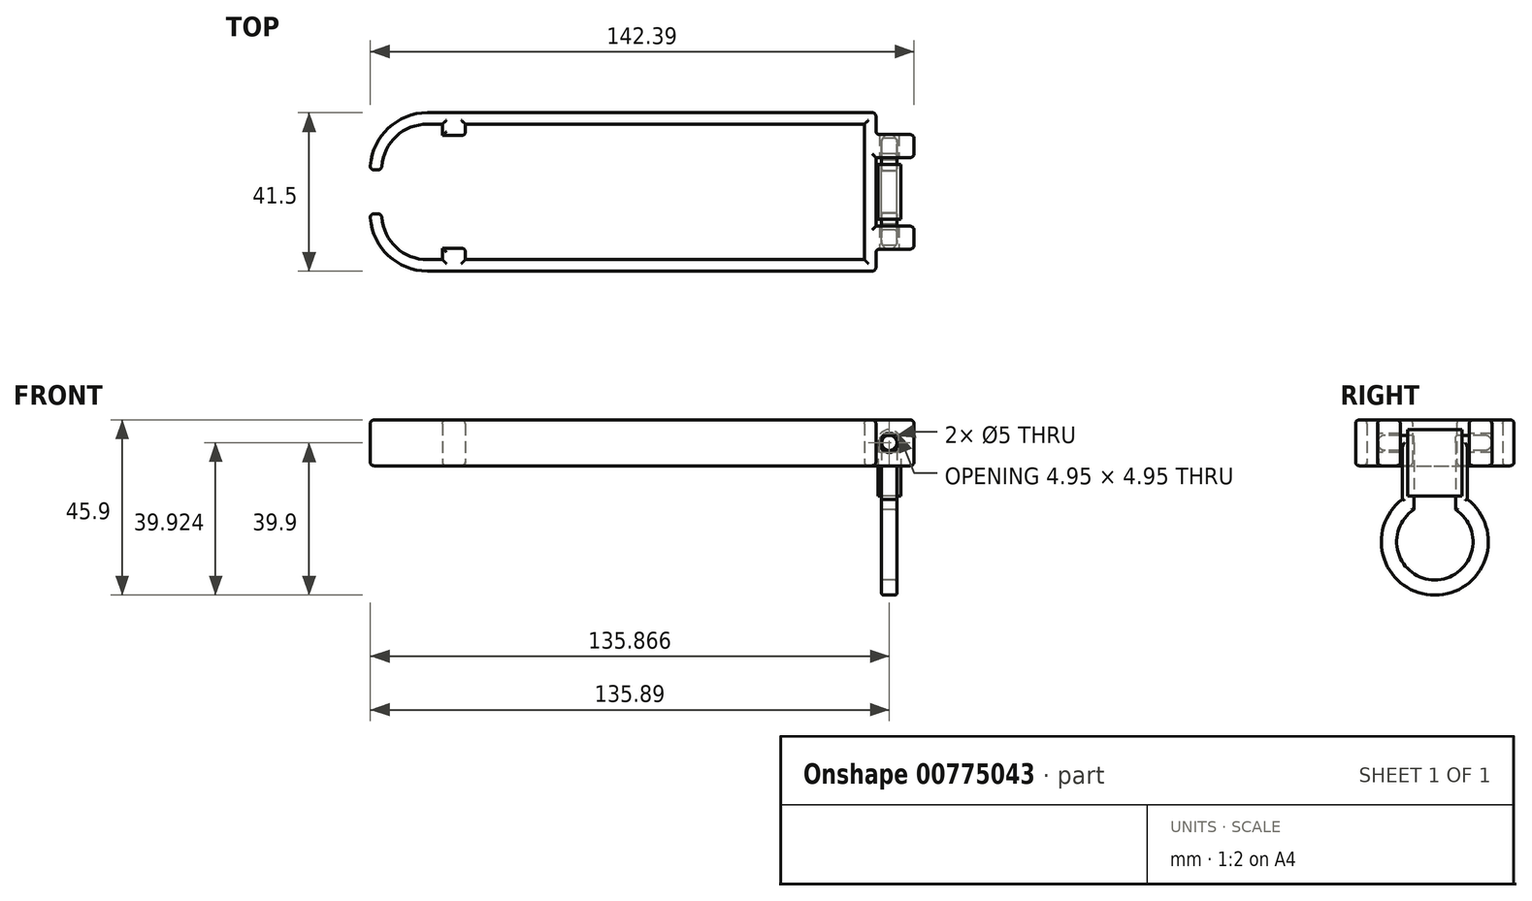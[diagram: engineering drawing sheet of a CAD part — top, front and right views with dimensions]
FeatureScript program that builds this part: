
annotation { "Feature Type Name" : "Feature", "Feature Type Description" : "" }
export const myFeature = defineFeature(function(context is Context, id is Id, definition is map)
    precondition{}
    {
        {
            var Q0;
            Q0=qCreatedBy(makeId("Top.planeOp"),FACE);
            var sketch = newSketch(context, id + "F0", { "sketchPlane" : qUnion([Q0])});
            skLineSegment(sketch, "E0.bottom", {"start": v(0, 0) * mm, "end": v(-104.5, 0) * mm, "construction": true});
            skLineSegment(sketch, "E0.top", {"start": v(0, -35.5) * mm, "end": v(-104.5, -35.5) * mm, "construction": true});
            skLineSegment(sketch, "E0.left", {"start": v(0, 0) * mm, "end": v(0, -35.5) * mm, "construction": true});
            skLineSegment(sketch, "E0.right", {"start": v(-104.5, 0) * mm, "end": v(-104.5, -3) * mm, "construction": true});
            skLineSegment(sketch, "E1.bottom", {"start": v(-104.5, -32.5) * mm, "end": v(-107.5, -32.5) * mm, "construction": true});
            skLineSegment(sketch, "E1.top", {"start": v(-104.5, -3) * mm, "end": v(-107.5, -3) * mm, "construction": true});
            skLineSegment(sketch, "E1.right", {"start": v(-107.5, -32.5) * mm, "end": v(-107.5, -19.25) * mm, "construction": true});
            skLineSegment(sketch, "E2.bottom", {"start": v(-107.5, -16.25) * mm, "end": v(-148.78, -16.25) * mm, "construction": true});
            skLineSegment(sketch, "E2.top", {"start": v(-107.5, -19.25) * mm, "end": v(-148.78, -19.25) * mm, "construction": true});
            skLineSegment(sketch, "E2.right", {"start": v(-148.78, -16.25) * mm, "end": v(-148.78, -19.25) * mm, "construction": true});
            skLineSegment(sketch, "E3.trimOffspring", {"start": v(-107.5, -16.25) * mm, "end": v(-107.5, -3) * mm, "construction": true});
            skLineSegment(sketch, "E4.trimOffspring", {"start": v(-104.5, -32.5) * mm, "end": v(-104.5, -35.5) * mm, "construction": true});
            skSolve(sketch);
        }
        {
            var Q0;
            Q0=qCreatedBy(makeId("Top.planeOp"),FACE);
            var sketch = newSketch(context, id + "F1", { "sketchPlane" : qUnion([Q0])});
            skLineSegment(sketch, "E5.bottom", {"start": v(0, 0) * mm, "end": v(-104.5, 0) * mm});
            skLineSegment(sketch, "E5.top", {"start": v(0, 3) * mm, "end": v(-114.42, 3) * mm});
            skLineSegment(sketch, "E5.left", {"start": v(0, 0) * mm, "end": v(0, 3) * mm});
            skLineSegment(sketch, "E6.bottom", {"start": v(0, -35.5) * mm, "end": v(-104.5, -35.5) * mm});
            skLineSegment(sketch, "E6.top", {"start": v(0, -38.5) * mm, "end": v(-114.42, -38.5) * mm});
            skLineSegment(sketch, "E6.left", {"start": v(0, -35.5) * mm, "end": v(0, -38.5) * mm});
            skLineSegment(sketch, "E7.top", {"start": v(-104.5, -3) * mm, "end": v(-110.5, -3) * mm});
            skLineSegment(sketch, "E7.left", {"start": v(-104.5, 0) * mm, "end": v(-104.5, -3) * mm});
            skLineSegment(sketch, "E7.right", {"start": v(-110.5, 0) * mm, "end": v(-110.5, -3) * mm});
            skLineSegment(sketch, "E8.top", {"start": v(-110.5, -32.5) * mm, "end": v(-104.5, -32.5) * mm});
            skLineSegment(sketch, "E8.left", {"start": v(-110.5, -35.5) * mm, "end": v(-110.5, -32.5) * mm});
            skLineSegment(sketch, "E8.right", {"start": v(-104.5, -35.5) * mm, "end": v(-104.5, -32.5) * mm});
            skArc(sketch, "E9", {"start": v(-114.42, 3) * mm, "mid": v(-125.03, -1.4) * mm, "end": v(-129.42, -12) * mm});
            skArc(sketch, "E10", {"start": v(-114.42, 0) * mm, "mid": v(-122.9, -3.51) * mm, "end": v(-126.42, -12) * mm});
            skLineSegment(sketch, "E11.bottom", {"start": v(-129.42, -12) * mm, "end": v(-126.42, -12) * mm});
            skArc(sketch, "E12", {"start": v(-129.42, -23.5) * mm, "mid": v(-125.03, -34.1) * mm, "end": v(-114.42, -38.5) * mm});
            skArc(sketch, "E13", {"start": v(-126.42, -23.5) * mm, "mid": v(-122.9, -31.99) * mm, "end": v(-114.42, -35.5) * mm});
            skLineSegment(sketch, "E14.bottom", {"start": v(-126.42, -23.5) * mm, "end": v(-129.42, -23.5) * mm});
            skLineSegment(sketch, "E15.trimOffspring", {"start": v(-110.5, -35.5) * mm, "end": v(-114.42, -35.5) * mm});
            skLineSegment(sketch, "E16.trimOffspring", {"start": v(-110.5, 0) * mm, "end": v(-114.42, 0) * mm});
            skLineSegment(sketch, "E17.bottom", {"start": v(0, -38.5) * mm, "end": v(3, -38.5) * mm});
            skLineSegment(sketch, "E17.top", {"start": v(0, 3) * mm, "end": v(3, 3) * mm});
            skLineSegment(sketch, "E17.left", {"start": v(0, -38.5) * mm, "end": v(0, 3) * mm});
            skLineSegment(sketch, "E17.right", {"start": v(3, -38.5) * mm, "end": v(3, -32.75) * mm});
            skLineSegment(sketch, "E18.bottom", {"start": v(13, -2.75) * mm, "end": v(3, -2.75) * mm});
            skLineSegment(sketch, "E18.top", {"start": v(13, -32.75) * mm, "end": v(3, -32.75) * mm});
            skLineSegment(sketch, "E19.bottom", {"start": v(3, -8.75) * mm, "end": v(13, -8.75) * mm});
            skLineSegment(sketch, "E19.top", {"start": v(3, -26.75) * mm, "end": v(13, -26.75) * mm});
            skPoint(sketch, "E19.middle", {"position": v(13, -17.75) * mm});
            skPoint(sketch, "E20.orphan", {"position": v(63.3, -6.49) * mm});
            skPoint(sketch, "E21.trimOffspring.end.orphan", {"position": v(63.3, -28.49) * mm});
            skLineSegment(sketch, "E22.trimOffspring", {"start": v(3, -26.75) * mm, "end": v(3, -8.75) * mm});
            skLineSegment(sketch, "E23.trimOffspring", {"start": v(3, -2.75) * mm, "end": v(3, 3) * mm});
            skLineSegment(sketch, "E24", {"start": v(13, -8.75) * mm, "end": v(13, -2.75) * mm});
            skLineSegment(sketch, "E25", {"start": v(13, -32.75) * mm, "end": v(13, -26.75) * mm});
            skSolve(sketch);
        }
        {
            var Q0;
            Q0=qSketchRegion(id+"F1",true);
            extrude(context, id + "F2", {"entities" : qUnion([Q0]), "depth" : 12 * mm, "offsetDistance" : 25 * mm});
        }
        {
            var Q0;
            Q0=qCreatedBy(makeId("Right.planeOp"),FACE);
            cPlane(context, id + "F3", {"entities" : qUnion([Q0]), "cplaneType" : CPlaneType.OFFSET, "offset" : 6.5 * mm, "width" : 150 * mm, "height" : 150 * mm});
        }
        {
            var Q0;
            Q0=makeQuery(id+"F2.opExtrude","SWEPT_FACE",FACE,{"disambiguationData":[OSD([sQuery(id+"F1.wireOp",EDGE,"E18.top")])]});
            var sketch = newSketch(context, id + "F4", { "sketchPlane" : qUnion([Q0])});
            skCircle(sketch, "E26", {"center": v(6.5, 6) * mm, "radius": 2.5 * mm});
            skSolve(sketch);
        }
        {
            var Q0;
            Q0 = qSketchRegion(id + "F4", true);
            var Q1;
            Q1=makeQuery(id+"F2.opExtrude","SWEPT_FACE",FACE,{"disambiguationData":[OSD([sQuery(id+"F1.wireOp",EDGE,"E18.bottom")])]});
            extrude(context, id + "F5", {"entities" : qUnion([Q0]), "operationType" : NewBodyOperationType.REMOVE, "endBound" : BoundingType.UP_TO_SURFACE, "oppositeDirection" : true, "depth" : 25 * mm, "endBoundEntityFace" : qUnion([Q1]), "offsetDistance" : 25 * mm});
        }
        {
            var Q0;
            Q0=makeQuery(id+"F2.opExtrude","SWEPT_EDGE",EDGE,{"disambiguationData":[OSD([sQuery(id+"F1.wireOp",EDGE,"E17.bottom"),sQuery(id+"F1.wireOp",EDGE,"E17.right")])]});
            var Q1;
            Q1=makeQuery(id+"F2.opExtrude","SWEPT_EDGE",EDGE,{"disambiguationData":[OSD([sQuery(id+"F1.wireOp",EDGE,"E17.right"),sQuery(id+"F1.wireOp",EDGE,"E18.top")])]});
            var Q2;
            Q2=makeQuery(id+"F2.opExtrude","SWEPT_EDGE",EDGE,{"disambiguationData":[OSD([sQuery(id+"F1.wireOp",EDGE,"E17.top"),sQuery(id+"F1.wireOp",EDGE,"E23.trimOffspring")])]});
            var Q3;
            Q3=makeQuery(id+"F2.opExtrude","CAP_FACE",FACE,{"disambiguationData":[OSD([sQuery(id+"F1.wireOp",EDGE,"E5.bottom"),sQuery(id+"F1.wireOp",EDGE,"E5.top"),sQuery(id+"F1.wireOp",EDGE,"E6.bottom"),sQuery(id+"F1.wireOp",EDGE,"E6.top"),sQuery(id+"F1.wireOp",EDGE,"E7.top"),sQuery(id+"F1.wireOp",EDGE,"E7.left"),sQuery(id+"F1.wireOp",EDGE,"E7.right"),sQuery(id+"F1.wireOp",EDGE,"E8.top"),sQuery(id+"F1.wireOp",EDGE,"E8.left"),sQuery(id+"F1.wireOp",EDGE,"E8.right"),sQuery(id+"F1.wireOp",EDGE,"E9"),sQuery(id+"F1.wireOp",EDGE,"E10"),sQuery(id+"F1.wireOp",EDGE,"E11.bottom"),sQuery(id+"F1.wireOp",EDGE,"E12"),sQuery(id+"F1.wireOp",EDGE,"E13"),sQuery(id+"F1.wireOp",EDGE,"E14.bottom"),sQuery(id+"F1.wireOp",EDGE,"E15.trimOffspring"),sQuery(id+"F1.wireOp",EDGE,"E16.trimOffspring"),sQuery(id+"F1.wireOp",EDGE,"E17.bottom"),sQuery(id+"F1.wireOp",EDGE,"E17.top"),sQuery(id+"F1.wireOp",EDGE,"E17.left"),sQuery(id+"F1.wireOp",EDGE,"E17.right"),sQuery(id+"F1.wireOp",EDGE,"xSZV2HGg-fjRU-nCpT-PhaE-ieglBuFw8G7T"),sQuery(id+"F1.wireOp",EDGE,"0Fs3mNXu-vN6e-gl2J-Gqjs-yi6b8POTL0Zl"),sQuery(id+"F1.wireOp",EDGE,"E18.bottom"),sQuery(id+"F1.wireOp",EDGE,"E18.top"),sQuery(id+"F1.wireOp",EDGE,"E19.bottom"),sQuery(id+"F1.wireOp",EDGE,"E19.top"),sQuery(id+"F1.wireOp",EDGE,"E22.trimOffspring"),sQuery(id+"F1.wireOp",EDGE,"E23.trimOffspring")])],"isStart":false});
            var Q4;
            Q4=makeQuery(id+"F2.opExtrude","SWEPT_EDGE",EDGE,{"disambiguationData":[OSD([sQuery(id+"F1.wireOp",EDGE,"E18.bottom"),sQuery(id+"F1.wireOp",EDGE,"E23.trimOffspring")])]});
            var Q5;
            Q5=makeQuery(id+"F2.opExtrude","SWEPT_FACE",FACE,{"disambiguationData":[OSD([sQuery(id+"F1.wireOp",EDGE,"E11.bottom")])]});
            var Q6;
            Q6=makeQuery(id+"F2.opExtrude","SWEPT_FACE",FACE,{"disambiguationData":[OSD([sQuery(id+"F1.wireOp",EDGE,"E14.bottom")])]});
            var Q7;
            Q7=makeQuery(id+"F2.opExtrude","SWEPT_EDGE",EDGE,{"disambiguationData":[OSD([sQuery(id+"F1.wireOp",EDGE,"E8.top"),sQuery(id+"F1.wireOp",EDGE,"E8.right")])]});
            var Q8;
            Q8=makeQuery(id+"F2.opExtrude","SWEPT_EDGE",EDGE,{"disambiguationData":[OSD([sQuery(id+"F1.wireOp",EDGE,"E7.top"),sQuery(id+"F1.wireOp",EDGE,"E7.left")])]});
            var Q9;
            Q9=makeQuery(id+"F2.opExtrude","SWEPT_FACE",FACE,{"disambiguationData":[OSD([sQuery(id+"F1.wireOp",EDGE,"E25")])]});
            var Q10;
            Q10=makeQuery(id+"F2.opExtrude","SWEPT_FACE",FACE,{"disambiguationData":[OSD([sQuery(id+"F1.wireOp",EDGE,"E24")])]});
            var Q11;
            Q11=makeQuery(id+"F2.opExtrude","CAP_FACE",FACE,{"disambiguationData":[OSD([sQuery(id+"F1.wireOp",EDGE,"E5.bottom"),sQuery(id+"F1.wireOp",EDGE,"E5.top"),sQuery(id+"F1.wireOp",EDGE,"E6.bottom"),sQuery(id+"F1.wireOp",EDGE,"E6.top"),sQuery(id+"F1.wireOp",EDGE,"E7.top"),sQuery(id+"F1.wireOp",EDGE,"E7.left"),sQuery(id+"F1.wireOp",EDGE,"E7.right"),sQuery(id+"F1.wireOp",EDGE,"E8.top"),sQuery(id+"F1.wireOp",EDGE,"E8.left"),sQuery(id+"F1.wireOp",EDGE,"E8.right"),sQuery(id+"F1.wireOp",EDGE,"E9"),sQuery(id+"F1.wireOp",EDGE,"E10"),sQuery(id+"F1.wireOp",EDGE,"E11.bottom"),sQuery(id+"F1.wireOp",EDGE,"E12"),sQuery(id+"F1.wireOp",EDGE,"E13"),sQuery(id+"F1.wireOp",EDGE,"E14.bottom"),sQuery(id+"F1.wireOp",EDGE,"E15.trimOffspring"),sQuery(id+"F1.wireOp",EDGE,"E16.trimOffspring"),sQuery(id+"F1.wireOp",EDGE,"E17.bottom"),sQuery(id+"F1.wireOp",EDGE,"E17.top"),sQuery(id+"F1.wireOp",EDGE,"E17.left"),sQuery(id+"F1.wireOp",EDGE,"E17.right"),sQuery(id+"F1.wireOp",EDGE,"E18.bottom"),sQuery(id+"F1.wireOp",EDGE,"E18.top"),sQuery(id+"F1.wireOp",EDGE,"E19.bottom"),sQuery(id+"F1.wireOp",EDGE,"E19.top"),sQuery(id+"F1.wireOp",EDGE,"E22.trimOffspring"),sQuery(id+"F1.wireOp",EDGE,"E23.trimOffspring"),sQuery(id+"F1.wireOp",EDGE,"E24"),sQuery(id+"F1.wireOp",EDGE,"E25")])],"isStart":true});
            fillet(context, id + "F6", {"entities" : qUnion([Q0, Q1, Q2, Q3, Q4, Q5, Q6, Q7, Q8, Q9, Q10, Q11]), "radius" : 1 * mm, "tangentPropagation" : true, "allowEdgeOverflow" : false});
        }
        {
            var Q0;
            Q0=qCreatedBy(id+"F3.planeOp",FACE);
            var sketch = newSketch(context, id + "F7", { "sketchPlane" : qUnion([Q0])});
            skLineSegment(sketch, "E27", {"start": v(-41.05, 6) * mm, "end": v(8.58, 6) * mm, "construction": true});
            skLineSegment(sketch, "E28", {"start": v(-17.75, 22.37) * mm, "end": v(-17.75, -44.39) * mm, "construction": true});
            skLineSegment(sketch, "E29", {"start": v(-26.75, 9.68) * mm, "end": v(-17.75, 9.68) * mm, "construction": true});
            skLineSegment(sketch, "E30", {"start": v(-17.75, 9.68) * mm, "end": v(-8.75, 9.68) * mm, "construction": true});
            skCircle(sketch, "E31", {"center": v(-17.75, -19.9) * mm, "radius": 10 * mm});
            skCircle(sketch, "E32", {"center": v(-17.75, -19.9) * mm, "radius": 14 * mm});
            skSolve(sketch);
        }
        {
            var Q0;
            Q0 = qSketchRegion(id + "F7", true);
            extrude(context, id + "F8", {"entities" : qUnion([Q0]), "depth" : 2 * mm, "offsetDistance" : 25 * mm, "hasSecondDirection" : true, "secondDirectionOppositeDirection" : true, "secondDirectionDepth" : 2 * mm});
        }
        {
            var Q0;
            Q0=makeQuery(id+"F4.imprint","IMPRINT",FACE,{"disambiguationData":[TD([[makeQuery(id+"F4.imprint","IMPRINT",EDGE,{"derivedFrom":sQuery(id+"F4.wireOp",EDGE,"E26")}),-1.0]])]});
            var sketch = newSketch(context, id + "F9", { "sketchPlane" : qUnion([Q0])});
            skCircle(sketch, "E33", {"center": v(6.5, 6) * mm, "radius": 2 * mm});
            skSolve(sketch);
        }
        {
            var Q0;
            Q0 = qSketchRegion(id + "F9", true);
            var Q1;
            Q1=makeQuery(id+"F2.opExtrude","SWEPT_FACE",FACE,{"disambiguationData":[OSD([sQuery(id+"F1.wireOp",EDGE,"E18.bottom")])]});
            extrude(context, id + "F10", {"entities" : qUnion([Q0]), "endBound" : BoundingType.UP_TO_SURFACE, "oppositeDirection" : true, "depth" : 25 * mm, "endBoundEntityFace" : qUnion([Q1]), "offsetDistance" : 25 * mm});
        }
        {
            var Q0;
            Q0=qCreatedBy(makeId("Top.planeOp"),FACE);
            var sketch = newSketch(context, id + "F11", { "sketchPlane" : qUnion([Q0])});
            skLineSegment(sketch, "E34.bottom", {"start": v(8.5, -9.25) * mm, "end": v(4.5, -9.25) * mm});
            skLineSegment(sketch, "E34.top", {"start": v(8.5, -26.25) * mm, "end": v(4.5, -26.25) * mm});
            skLineSegment(sketch, "E34.left", {"start": v(8.5, -9.25) * mm, "end": v(8.5, -26.25) * mm});
            skLineSegment(sketch, "E34.right", {"start": v(4.5, -9.25) * mm, "end": v(4.5, -26.25) * mm});
            skPoint(sketch, "E34.middle", {"position": v(6.5, -17.75) * mm});
            skSolve(sketch);
        }
        {
            var Q0;
            Q0 = qSketchRegion(id + "F11", true);
            var Q1;
            Q1=makeQuery(id+"F10.opExtrude","SWEPT_FACE",FACE,{"disambiguationData":[OSD([sQuery(id+"F9.wireOp",EDGE,"E33")])]});
            var Q2;
            Q2=makeQuery(id+"F8.opExtrude","SWEPT_FACE",FACE,{"disambiguationData":[OSD([sQuery(id+"F7.wireOp",EDGE,"E32")])]});
            extrude(context, id + "F12", {"entities" : qUnion([Q0]), "operationType" : NewBodyOperationType.ADD, "endBound" : BoundingType.UP_TO_SURFACE, "depth" : 25 * mm, "endBoundEntityFace" : qUnion([Q1]), "offsetDistance" : 25 * mm, "hasSecondDirection" : true, "secondDirectionBound" : SecondDirectionBoundingType.UP_TO_SURFACE, "secondDirectionOppositeDirection" : true, "secondDirectionDepth" : 25 * mm, "secondDirectionBoundEntityFace" : qUnion([Q2])});
        }
        {
            var Q0;
            Q0=qCreatedBy(id+"F3.planeOp",FACE);
            var sketch = newSketch(context, id + "F13", { "sketchPlane" : qUnion([Q0])});
            skLineSegment(sketch, "E35.bottom", {"start": v(-12.25, -20.8) * mm, "end": v(-23.25, -20.8) * mm});
            skLineSegment(sketch, "E35.top", {"start": v(-12.25, 14.87) * mm, "end": v(-23.25, 14.87) * mm});
            skLineSegment(sketch, "E35.left", {"start": v(-12.25, -20.8) * mm, "end": v(-12.25, 14.87) * mm});
            skLineSegment(sketch, "E35.right", {"start": v(-23.25, -20.8) * mm, "end": v(-23.25, 14.87) * mm});
            skPoint(sketch, "E35.middle", {"position": v(-17.75, -2.96) * mm});
            skSolve(sketch);
        }
        {
            var Q0;
            Q0 = qSketchRegion(id + "F13", true);
            var Q1;
            Q1=makeQuery(id+"F12.boolean.opBoolean","MERGE",FACE,{"derivedFrom":[makeQuery(id+"F8.opExtrude","CAP_FACE",FACE,{"disambiguationData":[OSD([sQuery(id+"F7.wireOp",EDGE,"E31"),sQuery(id+"F7.wireOp",EDGE,"E32")])],"isStart":true}),makeQuery(id+"F12.opExtrude","SWEPT_FACE",FACE,{"disambiguationData":[OSD([sQuery(id+"F11.wireOp",EDGE,"E34.right")])]})]});
            var Q2;
            Q2=makeQuery(id+"F12.boolean.opBoolean","MERGE",FACE,{"derivedFrom":[makeQuery(id+"F8.opExtrude","CAP_FACE",FACE,{"disambiguationData":[OSD([sQuery(id+"F7.wireOp",EDGE,"E31"),sQuery(id+"F7.wireOp",EDGE,"E32")])],"isStart":false}),makeQuery(id+"F12.opExtrude","SWEPT_FACE",FACE,{"disambiguationData":[OSD([sQuery(id+"F11.wireOp",EDGE,"E34.left")])]})]});
            extrude(context, id + "F14", {"entities" : qUnion([Q0]), "operationType" : NewBodyOperationType.REMOVE, "endBound" : BoundingType.UP_TO_SURFACE, "oppositeDirection" : true, "depth" : 25 * mm, "endBoundEntityFace" : qUnion([Q1]), "offsetDistance" : 25 * mm, "hasSecondDirection" : true, "secondDirectionBound" : SecondDirectionBoundingType.UP_TO_SURFACE, "secondDirectionOppositeDirection" : false, "secondDirectionDepth" : 25 * mm, "secondDirectionBoundEntityFace" : qUnion([Q2])});
        }
        {
            var Q0;
            Q0=makeQuery(id+"F12.boolean.opBoolean","MERGE",FACE,{"derivedFrom":[makeQuery(id+"F8.opExtrude","CAP_FACE",FACE,{"disambiguationData":[OSD([sQuery(id+"F7.wireOp",EDGE,"E31"),sQuery(id+"F7.wireOp",EDGE,"E32")])],"isStart":false}),makeQuery(id+"F12.opExtrude","SWEPT_FACE",FACE,{"disambiguationData":[OSD([sQuery(id+"F11.wireOp",EDGE,"E34.left")])]})]});
            var Q1;
            Q1=makeQuery(id+"F12.boolean.opBoolean","MERGE",FACE,{"derivedFrom":[makeQuery(id+"F8.opExtrude","CAP_FACE",FACE,{"disambiguationData":[OSD([sQuery(id+"F7.wireOp",EDGE,"E31"),sQuery(id+"F7.wireOp",EDGE,"E32")])],"isStart":true}),makeQuery(id+"F12.opExtrude","SWEPT_FACE",FACE,{"disambiguationData":[OSD([sQuery(id+"F11.wireOp",EDGE,"E34.right")])]})]});
            fillet(context, id + "F15", {"entities" : qUnion([Q0, Q1]), "radius" : .5 * mm, "tangentPropagation" : true, "allowEdgeOverflow" : false});
        }
        {
            var Q0;
            Q0=makeQuery(id+"F10.opExtrude","CAP_FACE",FACE,{"disambiguationData":[OSD([sQuery(id+"F9.wireOp",EDGE,"E33")])],"isStart":false});
            var Q1;
            Q1=makeQuery(id+"F10.opExtrude","CAP_FACE",FACE,{"disambiguationData":[OSD([sQuery(id+"F9.wireOp",EDGE,"E33")])],"isStart":true});
            fillet(context, id + "F16", {"entities" : qUnion([Q0, Q1]), "radius" : 2 * mm, "tangentPropagation" : true, "allowEdgeOverflow" : false});
        }
        {
            var Q0;
            Q0=qCreatedBy(id+"F3.planeOp",FACE);
            var sketch = newSketch(context, id + "F17", { "sketchPlane" : qUnion([Q0])});
            skLineSegment(sketch, "E36.bottom", {"start": v(-24.9, 9.5) * mm, "end": v(-10.6, 9.5) * mm});
            skLineSegment(sketch, "E36.top", {"start": v(-24.9, -7.88) * mm, "end": v(-10.6, -7.88) * mm});
            skLineSegment(sketch, "E36.left", {"start": v(-24.9, 9.5) * mm, "end": v(-24.9, -7.88) * mm});
            skLineSegment(sketch, "E36.right", {"start": v(-10.6, 9.5) * mm, "end": v(-10.6, -7.88) * mm});
            skPoint(sketch, "E36.middle", {"position": v(-17.75, 0.81) * mm});
            skLineSegment(sketch, "E37", {"start": v(-34.22, 8) * mm, "end": v(-2.5, 8) * mm, "construction": true});
            skSolve(sketch);
        }
        {
            var Q0;
            Q0 = qSketchRegion(id + "F17", true);
            extrude(context, id + "F18", {"entities" : qUnion([Q0]), "depth" : 3 * mm, "offsetDistance" : 25 * mm, "hasSecondDirection" : true, "secondDirectionOppositeDirection" : true, "secondDirectionDepth" : 3 * mm});
        }
        {
            var Q0;
            Q0=makeQuery(id+"F18.opExtrude","CAP_EDGE",EDGE,{"disambiguationData":[OSD([sQuery(id+"F17.wireOp",EDGE,"E36.bottom")])],"isStart":true});
            var Q1;
            Q1=makeQuery(id+"F18.opExtrude","CAP_EDGE",EDGE,{"disambiguationData":[OSD([sQuery(id+"F17.wireOp",EDGE,"E36.bottom")])],"isStart":false});
            fillet(context, id + "F19", {"entities" : qUnion([Q0, Q1]), "radius" : 3 * mm, "tangentPropagation" : true, "allowEdgeOverflow" : false});
        }
        {
            var Q0;
            Q0=makeQuery(id+"F8.opExtrude","SWEPT_BODY",BODY,{"disambiguationData":[OSD([sQuery(id+"F7.wireOp",EDGE,"E31"),sQuery(id+"F7.wireOp",EDGE,"E32")])]});
            var Q1;
            Q1=makeQuery(id+"F18.opExtrude","SWEPT_BODY",BODY,{"disambiguationData":[OSD([sQuery(id+"F17.wireOp",EDGE,"E36.bottom"),sQuery(id+"F17.wireOp",EDGE,"E36.top"),sQuery(id+"F17.wireOp",EDGE,"E36.left"),sQuery(id+"F17.wireOp",EDGE,"E36.right")])]});
            booleanBodies(context, id + "F20", {"operationType" : BooleanOperationType.SUBTRACTION, "tools" : qUnion([Q0]), "targets" : qUnion([Q1]), "keepTools" : true});
        }
    });
